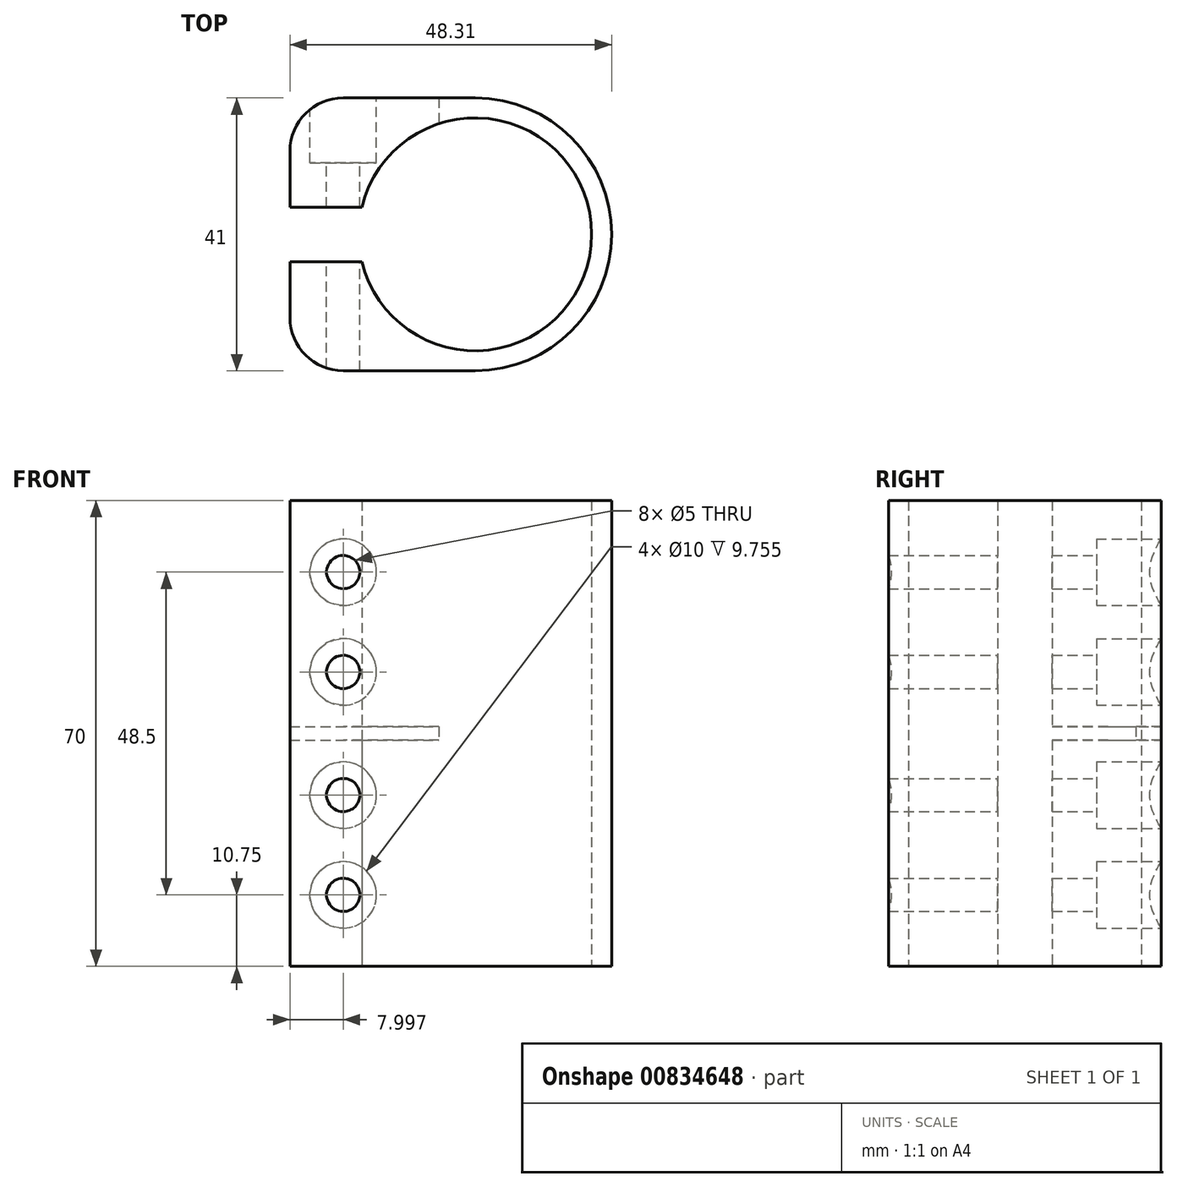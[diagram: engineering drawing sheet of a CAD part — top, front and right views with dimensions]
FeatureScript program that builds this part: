
annotation { "Feature Type Name" : "Feature", "Feature Type Description" : "" }
export const myFeature = defineFeature(function(context is Context, id is Id, definition is map)
    precondition{}
    {
        {
            var Q0;
            Q0=qCreatedBy(makeId("Top.planeOp"),FACE);
            var sketch = newSketch(context, id + "F0", { "sketchPlane" : qUnion([Q0])});
            skArc(sketch, "E0", {"start": v(-17.01, -4.1) * mm, "mid": v(17.5, 0) * mm, "end": v(-17.01, 4.1) * mm});
            skArc(sketch, "E1", {"start": v(0, -20.5) * mm, "mid": v(20.5, 0) * mm, "end": v(0, 20.5) * mm});
            skLineSegment(sketch, "E2", {"start": v(-17.01, 4.1) * mm, "end": v(-27.81, 4.1) * mm});
            skLineSegment(sketch, "E3", {"start": v(-27.81, 4.1) * mm, "end": v(-27.81, 12.5) * mm});
            skLineSegment(sketch, "E4", {"start": v(-19.81, 20.5) * mm, "end": v(0, 20.5) * mm});
            skPoint(sketch, "E5.visualSharp", {"position": v(-27.81, 20.5) * mm});
            skArc(sketch, "E5.filletArc", {"start": v(-19.81, 20.5) * mm, "mid": v(-25.47, 18.16) * mm, "end": v(-27.81, 12.5) * mm});
            skLineSegment(sketch, "E6.MirrorCS", {"start": v(-19.81, -20.5) * mm, "end": v(0, -20.5) * mm});
            skArc(sketch, "E7.MirrorCS", {"start": v(-19.81, -20.5) * mm, "mid": v(-25.47, -18.16) * mm, "end": v(-27.81, -12.5) * mm});
            skLineSegment(sketch, "E8.MirrorCS", {"start": v(-27.81, -4.1) * mm, "end": v(-27.81, -12.5) * mm});
            skLineSegment(sketch, "E9.MirrorCS", {"start": v(-17.01, -4.1) * mm, "end": v(-27.81, -4.1) * mm});
            skSolve(sketch);
        }
        {
            var Q0;
            Q0 = qSketchRegion(id + "F0", true);
            var Q1;
            Q1=makeQuery(id+"F0.imprint","IMPRINT",FACE,{"disambiguationData":[TD([[makeQuery(id+"F0.imprint","IMPRINT",EDGE,{"derivedFrom":sQuery(id+"F0.wireOp",EDGE,"E0")}),-1.0]])]});
            extrude(context, id + "F1", {"entities" : qUnion([Q0, Q1]), "endBound" : BoundingType.SYMMETRIC, "depth" : 70 * mm, "offsetDistance" : 25 * mm});
        }
        {
            var Q0;
            Q0=makeQuery(id+"F1.opExtrude","SWEPT_FACE",FACE,{"disambiguationData":[OSD([sQuery(id+"F0.wireOp",EDGE,"E4")])]});
            var sketch = newSketch(context, id + "F2", { "sketchPlane" : qUnion([Q0])});
            skPoint(sketch, "E10", {"position": v(19.81, -24.25) * mm});
            skPoint(sketch, "E11", {"position": v(19.81, -9.25) * mm});
            skPoint(sketch, "E12", {"position": v(19.81, 9.25) * mm});
            skPoint(sketch, "E13", {"position": v(19.81, 24.25) * mm});
            skSolve(sketch);
        }
        {
            var Q0;
            Q0=sQuery(id+"F2.wireOp",VERTEX,"E10");
            var Q1;
            Q1=sQuery(id+"F2.wireOp",VERTEX,"E11");
            var Q2;
            Q2=sQuery(id+"F2.wireOp",VERTEX,"E12");
            var Q3;
            Q3=sQuery(id+"F2.wireOp",VERTEX,"E13");
            var Q4;
            Q4=makeQuery(id+"F1.opExtrude","SWEPT_BODY",BODY,{"disambiguationData":[OSD([sQuery(id+"F0.wireOp",EDGE,"E0"),sQuery(id+"F0.wireOp",EDGE,"E1"),sQuery(id+"F0.wireOp",EDGE,"E2"),sQuery(id+"F0.wireOp",EDGE,"E3"),sQuery(id+"F0.wireOp",EDGE,"E4"),sQuery(id+"F0.wireOp",EDGE,"E5.filletArc"),sQuery(id+"F0.wireOp",EDGE,"E6.MirrorCS"),sQuery(id+"F0.wireOp",EDGE,"E7.MirrorCS"),sQuery(id+"F0.wireOp",EDGE,"E8.MirrorCS"),sQuery(id+"F0.wireOp",EDGE,"E9.MirrorCS")])]});
            hole(context, id + "F3", {"style" : HoleStyle.C_BORE, "endStyle" : HoleEndStyle.THROUGH, "holeDiameter" : 5 * mm, "cBoreDiameter" : 10 * mm, "cBoreDepth" : 8 * mm, "majorDiameter" : 5 * mm, "isTappedThrough" : true, "tappedDepth" : 12 * mm, "tapClearance" : 3, "locations" : qUnion([Q0, Q1, Q2, Q3]), "scope" : qUnion([Q4])});
        }
        {
            var Q0;
            Q0=qCreatedBy(makeId("Front.planeOp"),FACE);
            var sketch = newSketch(context, id + "F4", { "sketchPlane" : qUnion([Q0])});
            skLineSegment(sketch, "E14.bottom", {"start": v(-27.81, -1) * mm, "end": v(-5.41, -1) * mm});
            skLineSegment(sketch, "E14.top", {"start": v(-27.81, 1) * mm, "end": v(-5.41, 1) * mm});
            skLineSegment(sketch, "E14.left", {"start": v(-27.81, -1) * mm, "end": v(-27.81, 1) * mm});
            skLineSegment(sketch, "E14.right", {"start": v(-5.41, -1) * mm, "end": v(-5.41, 1) * mm});
            skSolve(sketch);
        }
        {
            var Q0;
            Q0 = qSketchRegion(id + "F4", true);
            extrude(context, id + "F5", {"entities" : qUnion([Q0]), "operationType" : NewBodyOperationType.REMOVE, "oppositeDirection" : true, "depth" : 25 * mm, "offsetDistance" : 25 * mm});
        }
    });
